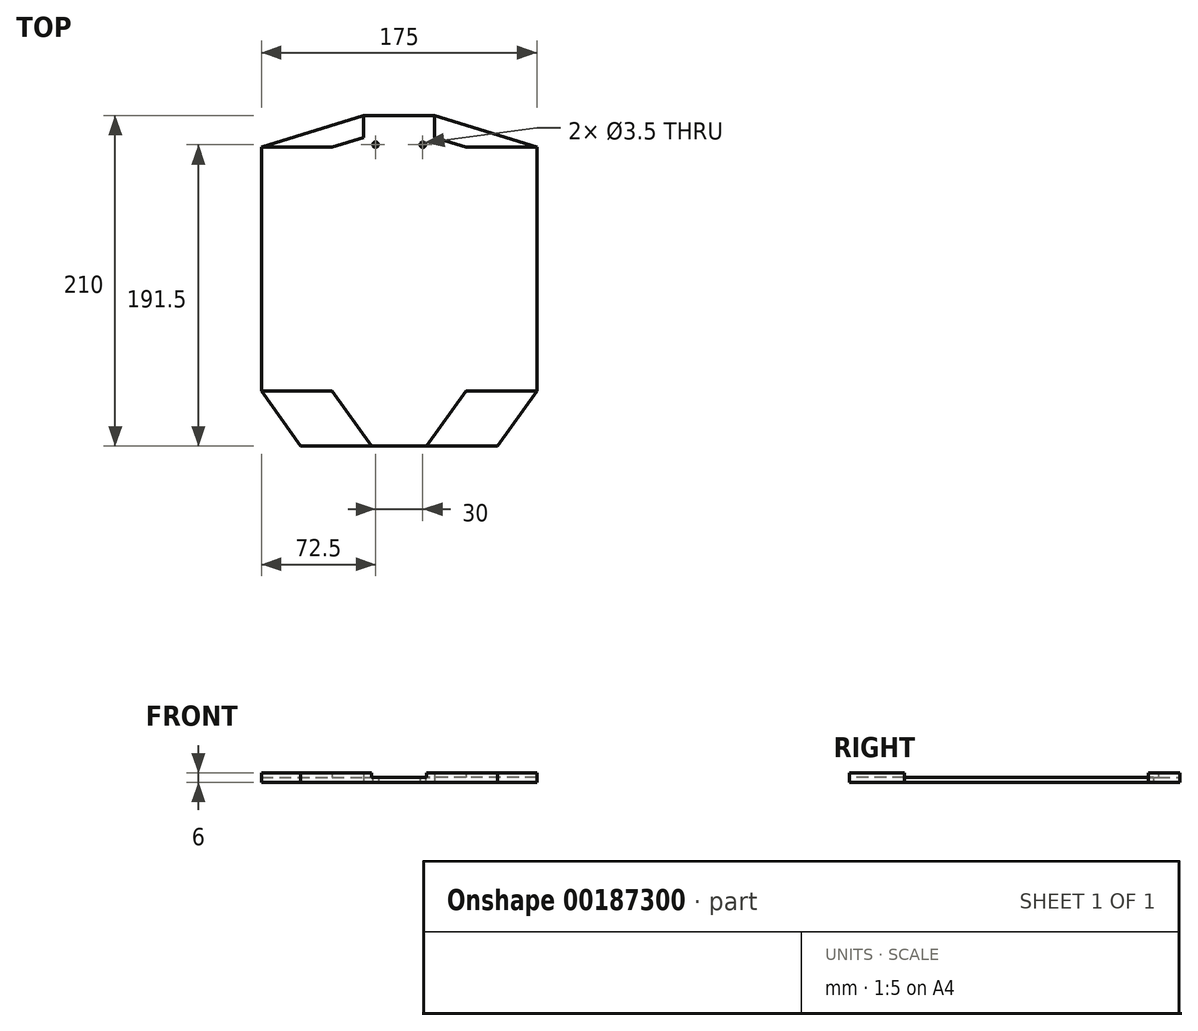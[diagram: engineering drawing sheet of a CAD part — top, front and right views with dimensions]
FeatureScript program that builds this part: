
annotation { "Feature Type Name" : "Feature", "Feature Type Description" : "" }
export const myFeature = defineFeature(function(context is Context, id is Id, definition is map)
    precondition{}
    {
        {
            var Q0;
            Q0=qCreatedBy(makeId("Top.planeOp"),FACE);
            var sketch = newSketch(context, id + "F0", { "sketchPlane" : qUnion([Q0])});
            skLineSegment(sketch, "E0", {"start": v(0, 20) * mm, "end": v(22.5, 20) * mm});
            skLineSegment(sketch, "E1", {"start": v(22.5, 20) * mm, "end": v(87.5, 0) * mm});
            skLineSegment(sketch, "E2", {"start": v(87.5, 0) * mm, "end": v(87.5, -155) * mm});
            skLineSegment(sketch, "E3", {"start": v(87.5, -155) * mm, "end": v(62.5, -190) * mm});
            skLineSegment(sketch, "E4", {"start": v(62.5, -190) * mm, "end": v(0, -190) * mm});
            skPoint(sketch, "E5.endSnap0", {"position": v(31.25, -190) * mm});
            skLineSegment(sketch, "E6", {"start": v(87.5, 0) * mm, "end": v(0, 0) * mm, "construction": true});
            skLineSegment(sketch, "E7.MirrorCS", {"start": v(-87.5, -155) * mm, "end": v(-62.5, -190) * mm});
            skLineSegment(sketch, "E8.MirrorCS", {"start": v(0, 20) * mm, "end": v(-22.5, 20) * mm});
            skLineSegment(sketch, "E9.MirrorCS", {"start": v(-87.5, 0) * mm, "end": v(0, 0) * mm, "construction": true});
            skLineSegment(sketch, "E10.MirrorCS", {"start": v(-22.5, 20) * mm, "end": v(-87.5, 0) * mm});
            skPoint(sketch, "E11.MirrorP", {"position": v(-31.25, -190) * mm});
            skLineSegment(sketch, "E12.MirrorCS", {"start": v(-87.5, 0) * mm, "end": v(-87.5, -155) * mm});
            skLineSegment(sketch, "E13.MirrorCS", {"start": v(-62.5, -190) * mm, "end": v(0, -190) * mm});
            skCircle(sketch, "E14", {"center": v(15, 1.5) * mm, "radius": 1.75 * mm});
            skCircle(sketch, "E15.MirrorC", {"center": v(-15, 1.5) * mm, "radius": 1.75 * mm});
            skSolve(sketch);
        }
        {
            var Q0;
            Q0 = qSketchRegion(id + "F0", true);
            extrude(context, id + "F1", {"entities" : qUnion([Q0]), "depth" : 3 * mm});
        }
        {
            var Q0;
            Q0=makeQuery(id+"F1.opExtrude","CAP_FACE",FACE,{"disambiguationData":[OSD([sQuery(id+"F0.wireOp",EDGE,"E0"),sQuery(id+"F0.wireOp",EDGE,"E1"),sQuery(id+"F0.wireOp",EDGE,"E2"),sQuery(id+"F0.wireOp",EDGE,"E3"),sQuery(id+"F0.wireOp",EDGE,"E4"),sQuery(id+"F0.wireOp",EDGE,"E7.MirrorCS"),sQuery(id+"F0.wireOp",EDGE,"E8.MirrorCS"),sQuery(id+"F0.wireOp",EDGE,"E10.MirrorCS"),sQuery(id+"F0.wireOp",EDGE,"E12.MirrorCS"),sQuery(id+"F0.wireOp",EDGE,"E13.MirrorCS"),sQuery(id+"F0.wireOp",EDGE,"E14"),sQuery(id+"F0.wireOp",EDGE,"E15.MirrorC")])],"isStart":false});
            var sketch = newSketch(context, id + "F2", { "sketchPlane" : qUnion([Q0])});
            skLineSegment(sketch, "E16", {"start": v(-22.5, 20) * mm, "end": v(-87.5, 0) * mm});
            skLineSegment(sketch, "E17", {"start": v(-87.5, 0) * mm, "end": v(-42.5, 0) * mm});
            skLineSegment(sketch, "E18", {"start": v(-42.5, 0) * mm, "end": v(-22.5, 6.15) * mm});
            skLineSegment(sketch, "E19", {"start": v(-22.5, 6.15) * mm, "end": v(-22.5, 20) * mm});
            skLineSegment(sketch, "E20", {"start": v(-87.5, -155) * mm, "end": v(-42.5, -155) * mm});
            skLineSegment(sketch, "E21", {"start": v(-42.5, -155) * mm, "end": v(-17.5, -190) * mm});
            skLineSegment(sketch, "E22.MirrorCS", {"start": v(22.5, 6.15) * mm, "end": v(22.5, 20) * mm});
            skLineSegment(sketch, "E23.MirrorCS", {"start": v(42.5, 0) * mm, "end": v(22.5, 6.15) * mm});
            skLineSegment(sketch, "E24.MirrorCS", {"start": v(87.5, 0) * mm, "end": v(42.5, 0) * mm});
            skLineSegment(sketch, "E25.MirrorCS", {"start": v(22.5, 20) * mm, "end": v(87.5, 0) * mm});
            skLineSegment(sketch, "E26.MirrorCS", {"start": v(42.5, -155) * mm, "end": v(17.5, -190) * mm});
            skLineSegment(sketch, "E27.MirrorCS", {"start": v(87.5, -155) * mm, "end": v(42.5, -155) * mm});
            skLineSegment(sketch, "E28", {"start": v(-87.5, -155) * mm, "end": v(-62.5, -190) * mm});
            skLineSegment(sketch, "E29", {"start": v(-62.5, -190) * mm, "end": v(-17.5, -190) * mm});
            skLineSegment(sketch, "E30.MirrorCS", {"start": v(87.5, -155) * mm, "end": v(62.5, -190) * mm});
            skLineSegment(sketch, "E31.MirrorCS", {"start": v(62.5, -190) * mm, "end": v(17.5, -190) * mm});
            skSolve(sketch);
        }
        {
            var Q0;
            Q0 = qSketchRegion(id + "F2", true);
            extrude(context, id + "F3", {"entities" : qUnion([Q0]), "operationType" : NewBodyOperationType.ADD, "depth" : 3 * mm});
        }
    });
